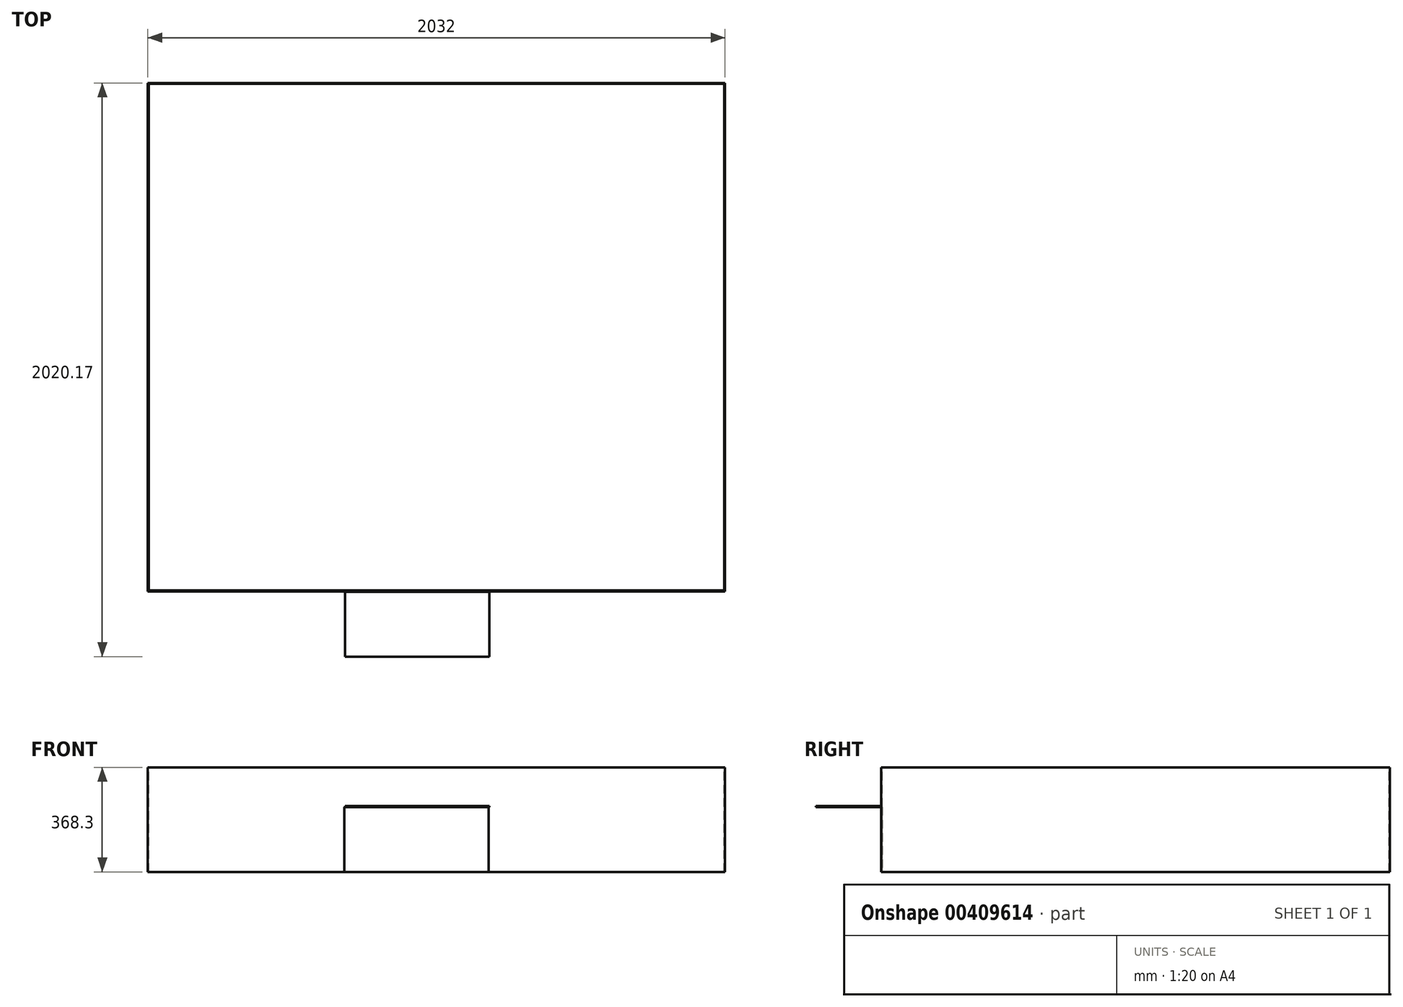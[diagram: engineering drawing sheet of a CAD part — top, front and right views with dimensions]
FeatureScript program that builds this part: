
annotation { "Feature Type Name" : "Feature", "Feature Type Description" : "" }
export const myFeature = defineFeature(function(context is Context, id is Id, definition is map)
    precondition{}
    {
        {
            var Q0;
            Q0=qCreatedBy(makeId("Top.planeOp"),FACE);
            var sketch = newSketch(context, id + "F0", { "sketchPlane" : qUnion([Q0])});
            skLineSegment(sketch, "E0.bottom", {"start": v(-1075.57, -643.32) * mm, "end": v(956.43, -643.32) * mm});
            skLineSegment(sketch, "E0.top", {"start": v(-1075.57, 1147.38) * mm, "end": v(956.43, 1147.38) * mm});
            skLineSegment(sketch, "E0.left", {"start": v(-1075.57, -643.32) * mm, "end": v(-1075.57, 1147.38) * mm});
            skLineSegment(sketch, "E0.right", {"start": v(956.43, -643.32) * mm, "end": v(956.43, 1147.38) * mm});
            skSolve(sketch);
        }
        {
            var Q0;
            Q0=makeQuery(id+"F0.imprint","IMPRINT",FACE,{"disambiguationData":[TD([[makeQuery(id+"F0.imprint","IMPRINT",EDGE,{"derivedFrom":sQuery(id+"F0.wireOp",EDGE,"E0.bottom")}),1.0]])]});
            extrude(context, id + "F1", {"entities" : qUnion([Q0]), "depth" : 368.3 * mm});
        }
        {
            var Q0;
            Q0=makeQuery(id+"F1.opExtrude","CAP_FACE",FACE,{"disambiguationData":[OSD([sQuery(id+"F0.wireOp",EDGE,"E0.bottom"),sQuery(id+"F0.wireOp",EDGE,"E0.top"),sQuery(id+"F0.wireOp",EDGE,"E0.left"),sQuery(id+"F0.wireOp",EDGE,"E0.right")])],"isStart":false});
            var sketch = newSketch(context, id + "F2", { "sketchPlane" : qUnion([Q0])});
            skLineSegment(sketch, "E1.bottom", {"start": v(-1072.4, 1144.2) * mm, "end": v(953.25, 1144.2) * mm});
            skLineSegment(sketch, "E1.top", {"start": v(-1072.4, -640.14) * mm, "end": v(953.25, -640.14) * mm});
            skLineSegment(sketch, "E1.left", {"start": v(-1072.4, 1144.2) * mm, "end": v(-1072.4, -640.14) * mm});
            skLineSegment(sketch, "E1.right", {"start": v(953.25, 1144.2) * mm, "end": v(953.25, -640.14) * mm});
            skSolve(sketch);
        }
        {
            var Q0;
            Q0=makeQuery(id+"F2.imprint","IMPRINT",FACE,{"disambiguationData":[TD([[makeQuery(id+"F2.imprint","IMPRINT",EDGE,{"derivedFrom":sQuery(id+"F2.wireOp",EDGE,"E1.bottom")}),-1.0]])]});
            extrude(context, id + "F3", {"entities" : qUnion([Q0]), "operationType" : NewBodyOperationType.REMOVE, "oppositeDirection" : true, "depth" : 368.3 * mm});
        }
        {
            var Q0;
            Q0=makeQuery(id+"F1.opExtrude","SWEPT_FACE",FACE,{"disambiguationData":[OSD([sQuery(id+"F0.wireOp",EDGE,"E0.bottom")])]});
            var sketch = newSketch(context, id + "F4", { "sketchPlane" : qUnion([Q0])});
            skLineSegment(sketch, "E2.bottom", {"start": v(-383.32, 228.6) * mm, "end": v(124.68, 228.6) * mm});
            skLineSegment(sketch, "E2.top", {"start": v(-383.32, 0) * mm, "end": v(124.68, 0) * mm});
            skLineSegment(sketch, "E2.left", {"start": v(-383.32, 228.6) * mm, "end": v(-383.32, 0) * mm});
            skLineSegment(sketch, "E2.right", {"start": v(124.68, 228.6) * mm, "end": v(124.68, 0) * mm});
            skSolve(sketch);
        }
        {
            var Q0;
            Q0=makeQuery(id+"F4.imprint","IMPRINT",FACE,{"disambiguationData":[TD([[makeQuery(id+"F4.imprint","IMPRINT",EDGE,{"derivedFrom":sQuery(id+"F4.wireOp",EDGE,"E2.bottom")}),-1.0]])]});
            extrude(context, id + "F5", {"entities" : qUnion([Q0]), "operationType" : NewBodyOperationType.REMOVE, "oppositeDirection" : true, "depth" : 25.4 * mm});
        }
        {
            var Q0;
            Q0=qCreatedBy(makeId("Top.planeOp"),FACE);
            cPlane(context, id + "F6", {"entities" : qUnion([Q0]), "cplaneType" : CPlaneType.OFFSET, "offset" : 228.6 * mm, "width" : 152.4 * mm, "height" : 152.4 * mm});
        }
        {
            var Q0;
            Q0=qCreatedBy(id+"F6.planeOp",FACE);
            var sketch = newSketch(context, id + "F7", { "sketchPlane" : qUnion([Q0])});
            skLineSegment(sketch, "E3.bottom", {"start": v(-380.92, -644.19) * mm, "end": v(127.08, -644.19) * mm});
            skLineSegment(sketch, "E3.top", {"start": v(-380.92, -872.79) * mm, "end": v(127.08, -872.79) * mm});
            skLineSegment(sketch, "E3.left", {"start": v(-380.92, -644.19) * mm, "end": v(-380.92, -872.79) * mm});
            skLineSegment(sketch, "E3.right", {"start": v(127.08, -644.19) * mm, "end": v(127.08, -872.79) * mm});
            skSolve(sketch);
        }
        {
            var Q0;
            Q0 = qSketchRegion(id + "F7", true);
            extrude(context, id + "F8", {"entities" : qUnion([Q0]), "depth" : 3.17 * mm});
        }
    });
